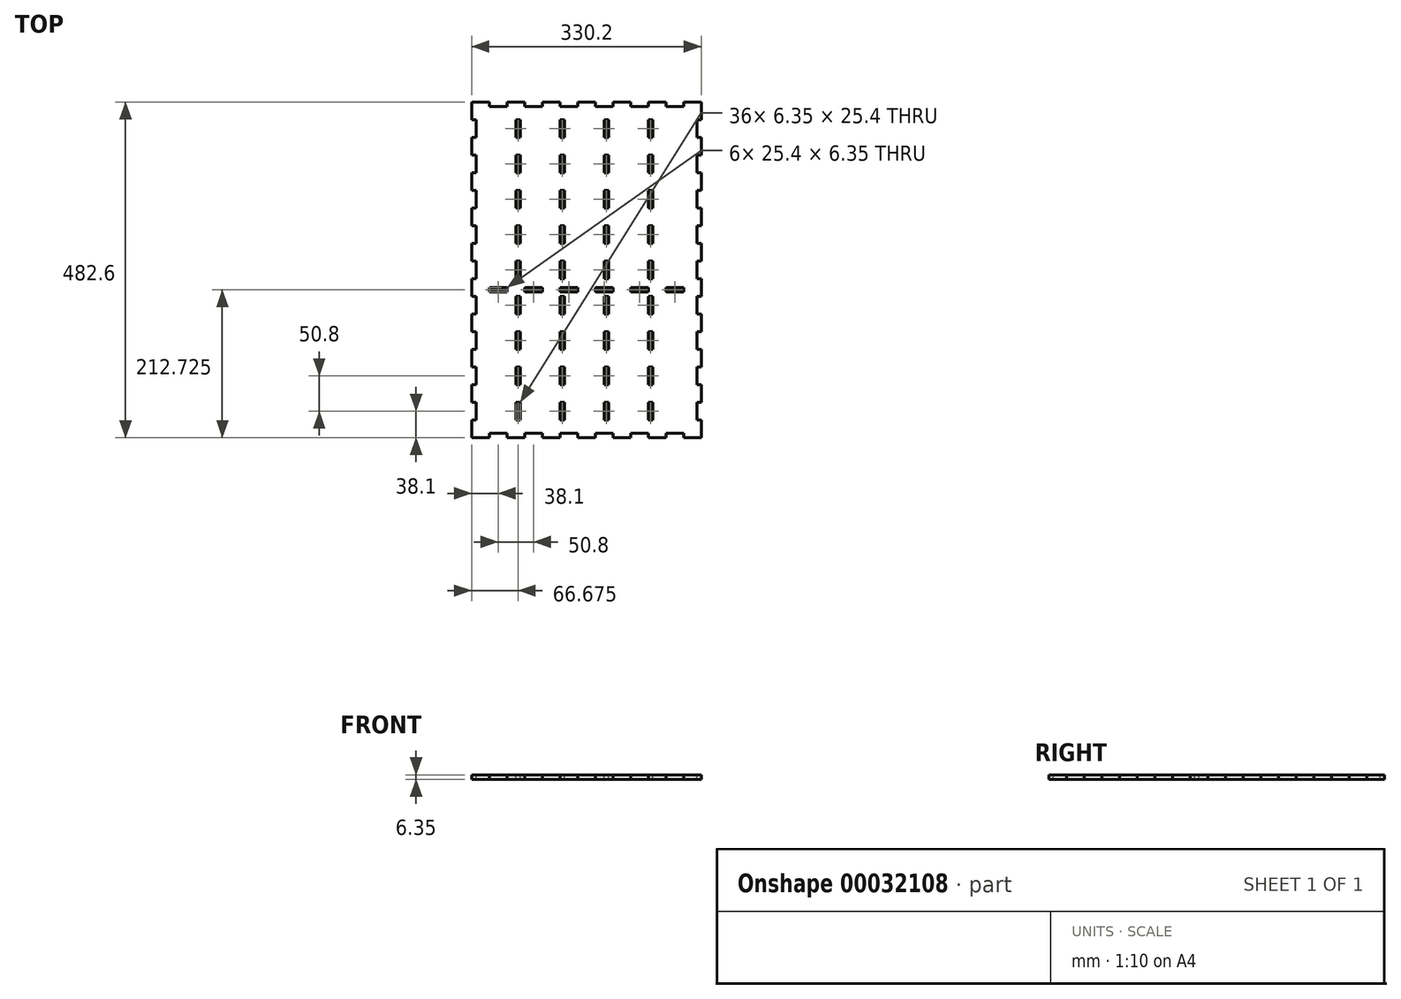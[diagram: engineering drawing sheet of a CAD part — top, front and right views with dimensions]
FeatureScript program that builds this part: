
annotation { "Feature Type Name" : "Feature", "Feature Type Description" : "" }
export const myFeature = defineFeature(function(context is Context, id is Id, definition is map)
    precondition{}
    {
        {
            var Q0;
            Q0=qCreatedBy(makeId("Top.planeOp"),FACE);
            var sketch = newSketch(context, id + "F0", { "sketchPlane" : qUnion([Q0])});
            skLineSegment(sketch, "E0.rect.bottom", {"start": v(165.1, 241.3) * mm, "end": v(-165.1, 241.3) * mm});
            skLineSegment(sketch, "E0.rect.top", {"start": v(165.1, -241.3) * mm, "end": v(-165.1, -241.3) * mm});
            skLineSegment(sketch, "E0.rect.left", {"start": v(165.1, 241.3) * mm, "end": v(165.1, -241.3) * mm});
            skLineSegment(sketch, "E0.rect.right", {"start": v(-165.1, 241.3) * mm, "end": v(-165.1, -241.3) * mm});
            skPoint(sketch, "E0.rect.middle", {"position": v(0, 0) * mm});
            skSolve(sketch);
        }
        {
            var Q0;
            Q0=makeQuery(id+"F0.imprint","IMPRINT",FACE,{"disambiguationData":[TD([[makeQuery(id+"F0.imprint","IMPRINT",EDGE,{"derivedFrom":sQuery(id+"F0.wireOp",EDGE,"E0.rect.bottom")}),1.0]])]});
            extrude(context, id + "F1", {"entities" : qUnion([Q0]), "depth" : 6.35 * mm});
        }
        {
            var Q0;
            Q0=makeQuery(id+"F1.opExtrude","CAP_FACE",FACE,{"disambiguationData":[OSD([sQuery(id+"F0.wireOp",EDGE,"E0.rect.bottom"),sQuery(id+"F0.wireOp",EDGE,"E0.rect.top"),sQuery(id+"F0.wireOp",EDGE,"E0.rect.left"),sQuery(id+"F0.wireOp",EDGE,"E0.rect.right")])],"isStart":false});
            var sketch = newSketch(context, id + "F2", { "sketchPlane" : qUnion([Q0])});
            skLineSegment(sketch, "E1.bottom", {"start": v(165.1, -215.9) * mm, "end": v(158.75, -215.9) * mm});
            skLineSegment(sketch, "E1.top", {"start": v(165.1, -190.5) * mm, "end": v(158.75, -190.5) * mm});
            skLineSegment(sketch, "E1.left", {"start": v(165.1, -215.9) * mm, "end": v(165.1, -190.5) * mm});
            skLineSegment(sketch, "E1.right", {"start": v(158.75, -215.9) * mm, "end": v(158.75, -190.5) * mm});
            skLineSegment(sketch, "E2.1.0.0", {"start": v(165.1, -165.1) * mm, "end": v(165.1, -139.7) * mm});
            skLineSegment(sketch, "E2.1.0.1", {"start": v(158.75, -165.1) * mm, "end": v(158.75, -139.7) * mm});
            skLineSegment(sketch, "E2.1.0.2", {"start": v(165.1, -165.1) * mm, "end": v(158.75, -165.1) * mm});
            skLineSegment(sketch, "E2.1.0.3", {"start": v(165.1, -139.7) * mm, "end": v(158.75, -139.7) * mm});
            skLineSegment(sketch, "E2.2.0.0", {"start": v(165.1, -114.3) * mm, "end": v(165.1, -88.9) * mm});
            skLineSegment(sketch, "E2.2.0.1", {"start": v(158.75, -114.3) * mm, "end": v(158.75, -88.9) * mm});
            skLineSegment(sketch, "E2.2.0.2", {"start": v(165.1, -114.3) * mm, "end": v(158.75, -114.3) * mm});
            skLineSegment(sketch, "E2.2.0.3", {"start": v(165.1, -88.9) * mm, "end": v(158.75, -88.9) * mm});
            skLineSegment(sketch, "E2.3.0.0", {"start": v(165.1, -63.5) * mm, "end": v(165.1, -38.1) * mm});
            skLineSegment(sketch, "E2.3.0.1", {"start": v(158.75, -63.5) * mm, "end": v(158.75, -38.1) * mm});
            skLineSegment(sketch, "E2.3.0.2", {"start": v(165.1, -63.5) * mm, "end": v(158.75, -63.5) * mm});
            skLineSegment(sketch, "E2.3.0.3", {"start": v(165.1, -38.1) * mm, "end": v(158.75, -38.1) * mm});
            skLineSegment(sketch, "E2.4.0.0", {"start": v(165.1, -12.7) * mm, "end": v(165.1, 12.7) * mm});
            skLineSegment(sketch, "E2.4.0.1", {"start": v(158.75, -12.7) * mm, "end": v(158.75, 12.7) * mm});
            skLineSegment(sketch, "E2.4.0.2", {"start": v(165.1, -12.7) * mm, "end": v(158.75, -12.7) * mm});
            skLineSegment(sketch, "E2.4.0.3", {"start": v(165.1, 12.7) * mm, "end": v(158.75, 12.7) * mm});
            skLineSegment(sketch, "E2.5.0.0", {"start": v(165.1, 38.1) * mm, "end": v(165.1, 63.5) * mm});
            skLineSegment(sketch, "E2.5.0.1", {"start": v(158.75, 38.1) * mm, "end": v(158.75, 63.5) * mm});
            skLineSegment(sketch, "E2.5.0.2", {"start": v(165.1, 38.1) * mm, "end": v(158.75, 38.1) * mm});
            skLineSegment(sketch, "E2.5.0.3", {"start": v(165.1, 63.5) * mm, "end": v(158.75, 63.5) * mm});
            skLineSegment(sketch, "E2.6.0.0", {"start": v(165.1, 88.9) * mm, "end": v(165.1, 114.3) * mm});
            skLineSegment(sketch, "E2.6.0.1", {"start": v(158.75, 88.9) * mm, "end": v(158.75, 114.3) * mm});
            skLineSegment(sketch, "E2.6.0.2", {"start": v(165.1, 88.9) * mm, "end": v(158.75, 88.9) * mm});
            skLineSegment(sketch, "E2.6.0.3", {"start": v(165.1, 114.3) * mm, "end": v(158.75, 114.3) * mm});
            skLineSegment(sketch, "E2.7.0.0", {"start": v(165.1, 139.7) * mm, "end": v(165.1, 165.1) * mm});
            skLineSegment(sketch, "E2.7.0.1", {"start": v(158.75, 139.7) * mm, "end": v(158.75, 165.1) * mm});
            skLineSegment(sketch, "E2.7.0.2", {"start": v(165.1, 139.7) * mm, "end": v(158.75, 139.7) * mm});
            skLineSegment(sketch, "E2.7.0.3", {"start": v(165.1, 165.1) * mm, "end": v(158.75, 165.1) * mm});
            skLineSegment(sketch, "E2.8.0.0", {"start": v(165.1, 190.5) * mm, "end": v(165.1, 215.9) * mm});
            skLineSegment(sketch, "E2.8.0.1", {"start": v(158.75, 190.5) * mm, "end": v(158.75, 215.9) * mm});
            skLineSegment(sketch, "E2.8.0.2", {"start": v(165.1, 190.5) * mm, "end": v(158.75, 190.5) * mm});
            skLineSegment(sketch, "E2.8.0.3", {"start": v(165.1, 215.9) * mm, "end": v(158.75, 215.9) * mm});
            skLineSegment(sketch, "E2.direction1", {"start": v(165.1, -215.9) * mm, "end": v(165.1, -165.1) * mm, "construction": true});
            skLineSegment(sketch, "E3", {"start": v(0, -241.3) * mm, "end": v(0, 241.3) * mm, "construction": true});
            skLineSegment(sketch, "E4.MirrorCS", {"start": v(-165.1, -215.9) * mm, "end": v(-158.75, -215.9) * mm});
            skLineSegment(sketch, "E5.MirrorCS", {"start": v(-165.1, -165.1) * mm, "end": v(-158.75, -165.1) * mm});
            skLineSegment(sketch, "E6.MirrorCS", {"start": v(-165.1, 12.7) * mm, "end": v(-158.75, 12.7) * mm});
            skLineSegment(sketch, "E7.MirrorCS", {"start": v(-165.1, -63.5) * mm, "end": v(-158.75, -63.5) * mm});
            skLineSegment(sketch, "E8.MirrorCS", {"start": v(-165.1, 63.5) * mm, "end": v(-158.75, 63.5) * mm});
            skLineSegment(sketch, "E9.MirrorCS", {"start": v(-165.1, -38.1) * mm, "end": v(-158.75, -38.1) * mm});
            skLineSegment(sketch, "E10.MirrorCS", {"start": v(-165.1, 38.1) * mm, "end": v(-158.75, 38.1) * mm});
            skLineSegment(sketch, "E11.MirrorCS", {"start": v(-165.1, -190.5) * mm, "end": v(-158.75, -190.5) * mm});
            skLineSegment(sketch, "E12.MirrorCS", {"start": v(-165.1, 215.9) * mm, "end": v(-158.75, 215.9) * mm});
            skLineSegment(sketch, "E13.MirrorCS", {"start": v(-165.1, 114.3) * mm, "end": v(-158.75, 114.3) * mm});
            skLineSegment(sketch, "E14.MirrorCS", {"start": v(-165.1, -12.7) * mm, "end": v(-158.75, -12.7) * mm});
            skLineSegment(sketch, "E15.MirrorCS", {"start": v(-165.1, 190.5) * mm, "end": v(-158.75, 190.5) * mm});
            skLineSegment(sketch, "E16.MirrorCS", {"start": v(-165.1, 88.9) * mm, "end": v(-158.75, 88.9) * mm});
            skLineSegment(sketch, "E17.MirrorCS", {"start": v(-165.1, -88.9) * mm, "end": v(-158.75, -88.9) * mm});
            skLineSegment(sketch, "E18.MirrorCS", {"start": v(-165.1, -139.7) * mm, "end": v(-158.75, -139.7) * mm});
            skLineSegment(sketch, "E19.MirrorCS", {"start": v(-165.1, -114.3) * mm, "end": v(-158.75, -114.3) * mm});
            skLineSegment(sketch, "E20.MirrorCS", {"start": v(-165.1, 139.7) * mm, "end": v(-158.75, 139.7) * mm});
            skLineSegment(sketch, "E21.MirrorCS", {"start": v(-165.1, 165.1) * mm, "end": v(-158.75, 165.1) * mm});
            skLineSegment(sketch, "E22.MirrorCS", {"start": v(-165.1, 88.9) * mm, "end": v(-165.1, 114.3) * mm});
            skLineSegment(sketch, "E23.MirrorCS", {"start": v(-158.75, 190.5) * mm, "end": v(-158.75, 215.9) * mm});
            skLineSegment(sketch, "E24.MirrorCS", {"start": v(-158.75, -12.7) * mm, "end": v(-158.75, 12.7) * mm});
            skLineSegment(sketch, "E25.MirrorCS", {"start": v(-165.1, -12.7) * mm, "end": v(-165.1, 12.7) * mm});
            skLineSegment(sketch, "E26.MirrorCS", {"start": v(-158.75, -63.5) * mm, "end": v(-158.75, -38.1) * mm});
            skLineSegment(sketch, "E27.MirrorCS", {"start": v(-165.1, 190.5) * mm, "end": v(-165.1, 215.9) * mm});
            skLineSegment(sketch, "E28.MirrorCS", {"start": v(-165.1, -215.9) * mm, "end": v(-165.1, -190.5) * mm});
            skLineSegment(sketch, "E29.MirrorCS", {"start": v(-158.75, -215.9) * mm, "end": v(-158.75, -190.5) * mm});
            skLineSegment(sketch, "E30.MirrorCS", {"start": v(-165.1, -114.3) * mm, "end": v(-165.1, -88.9) * mm});
            skLineSegment(sketch, "E31.MirrorCS", {"start": v(-165.1, 38.1) * mm, "end": v(-165.1, 63.5) * mm});
            skLineSegment(sketch, "E32.MirrorCS", {"start": v(-158.75, 38.1) * mm, "end": v(-158.75, 63.5) * mm});
            skLineSegment(sketch, "E33.MirrorCS", {"start": v(-165.1, -63.5) * mm, "end": v(-165.1, -38.1) * mm});
            skLineSegment(sketch, "E34.MirrorCS", {"start": v(-165.1, 139.7) * mm, "end": v(-165.1, 165.1) * mm});
            skLineSegment(sketch, "E35.MirrorCS", {"start": v(-158.75, 88.9) * mm, "end": v(-158.75, 114.3) * mm});
            skLineSegment(sketch, "E36.MirrorCS", {"start": v(-158.75, -114.3) * mm, "end": v(-158.75, -88.9) * mm});
            skLineSegment(sketch, "E37.MirrorCS", {"start": v(-158.75, -165.1) * mm, "end": v(-158.75, -139.7) * mm});
            skLineSegment(sketch, "E38.MirrorCS", {"start": v(-165.1, -165.1) * mm, "end": v(-165.1, -139.7) * mm});
            skLineSegment(sketch, "E39.MirrorCS", {"start": v(-158.75, 139.7) * mm, "end": v(-158.75, 165.1) * mm});
            skLineSegment(sketch, "E40.bottom", {"start": v(-139.7, -241.3) * mm, "end": v(-114.3, -241.3) * mm});
            skLineSegment(sketch, "E40.top", {"start": v(-139.7, -234.95) * mm, "end": v(-114.3, -234.95) * mm});
            skLineSegment(sketch, "E40.left", {"start": v(-139.7, -241.3) * mm, "end": v(-139.7, -234.95) * mm});
            skLineSegment(sketch, "E40.right", {"start": v(-114.3, -241.3) * mm, "end": v(-114.3, -234.95) * mm});
            skLineSegment(sketch, "E41", {"start": v(-165.1, 0) * mm, "end": v(165.1, 0) * mm, "construction": true});
            skLineSegment(sketch, "E42.0.1.0", {"start": v(-139.7, -31.75) * mm, "end": v(-139.7, -25.4) * mm});
            skLineSegment(sketch, "E42.0.1.1", {"start": v(-114.3, -31.75) * mm, "end": v(-114.3, -25.4) * mm});
            skLineSegment(sketch, "E42.0.1.2", {"start": v(-139.7, -25.4) * mm, "end": v(-114.3, -25.4) * mm});
            skLineSegment(sketch, "E42.0.1.3", {"start": v(-139.7, -31.75) * mm, "end": v(-114.3, -31.75) * mm});
            skLineSegment(sketch, "E42.1.0.0", {"start": v(-88.9, -241.3) * mm, "end": v(-88.9, -234.95) * mm});
            skLineSegment(sketch, "E42.1.0.1", {"start": v(-63.5, -241.3) * mm, "end": v(-63.5, -234.95) * mm});
            skLineSegment(sketch, "E42.1.0.2", {"start": v(-88.9, -234.95) * mm, "end": v(-63.5, -234.95) * mm});
            skLineSegment(sketch, "E42.1.0.3", {"start": v(-88.9, -241.3) * mm, "end": v(-63.5, -241.3) * mm});
            skLineSegment(sketch, "E42.1.1.0", {"start": v(-88.9, -31.75) * mm, "end": v(-88.9, -25.4) * mm});
            skLineSegment(sketch, "E42.1.1.1", {"start": v(-63.5, -31.75) * mm, "end": v(-63.5, -25.4) * mm});
            skLineSegment(sketch, "E42.1.1.2", {"start": v(-88.9, -25.4) * mm, "end": v(-63.5, -25.4) * mm});
            skLineSegment(sketch, "E42.1.1.3", {"start": v(-88.9, -31.75) * mm, "end": v(-63.5, -31.75) * mm});
            skLineSegment(sketch, "E42.2.0.0", {"start": v(-38.1, -241.3) * mm, "end": v(-38.1, -234.95) * mm});
            skLineSegment(sketch, "E42.2.0.1", {"start": v(-12.7, -241.3) * mm, "end": v(-12.7, -234.95) * mm});
            skLineSegment(sketch, "E42.2.0.2", {"start": v(-38.1, -234.95) * mm, "end": v(-12.7, -234.95) * mm});
            skLineSegment(sketch, "E42.2.0.3", {"start": v(-38.1, -241.3) * mm, "end": v(-12.7, -241.3) * mm});
            skLineSegment(sketch, "E42.2.1.0", {"start": v(-38.1, -31.75) * mm, "end": v(-38.1, -25.4) * mm});
            skLineSegment(sketch, "E42.2.1.1", {"start": v(-12.7, -31.75) * mm, "end": v(-12.7, -25.4) * mm});
            skLineSegment(sketch, "E42.2.1.2", {"start": v(-38.1, -25.4) * mm, "end": v(-12.7, -25.4) * mm});
            skLineSegment(sketch, "E42.2.1.3", {"start": v(-38.1, -31.75) * mm, "end": v(-12.7, -31.75) * mm});
            skLineSegment(sketch, "E42.3.0.0", {"start": v(12.7, -241.3) * mm, "end": v(12.7, -234.95) * mm});
            skLineSegment(sketch, "E42.3.0.1", {"start": v(38.1, -241.3) * mm, "end": v(38.1, -234.95) * mm});
            skLineSegment(sketch, "E42.3.0.2", {"start": v(12.7, -234.95) * mm, "end": v(38.1, -234.95) * mm});
            skLineSegment(sketch, "E42.3.0.3", {"start": v(12.7, -241.3) * mm, "end": v(38.1, -241.3) * mm});
            skLineSegment(sketch, "E42.3.1.0", {"start": v(12.7, -31.75) * mm, "end": v(12.7, -25.4) * mm});
            skLineSegment(sketch, "E42.3.1.1", {"start": v(38.1, -31.75) * mm, "end": v(38.1, -25.4) * mm});
            skLineSegment(sketch, "E42.3.1.2", {"start": v(12.7, -25.4) * mm, "end": v(38.1, -25.4) * mm});
            skLineSegment(sketch, "E42.3.1.3", {"start": v(12.7, -31.75) * mm, "end": v(38.1, -31.75) * mm});
            skLineSegment(sketch, "E42.4.0.0", {"start": v(63.5, -241.3) * mm, "end": v(63.5, -234.95) * mm});
            skLineSegment(sketch, "E42.4.0.1", {"start": v(88.9, -241.3) * mm, "end": v(88.9, -234.95) * mm});
            skLineSegment(sketch, "E42.4.0.2", {"start": v(63.5, -234.95) * mm, "end": v(88.9, -234.95) * mm});
            skLineSegment(sketch, "E42.4.0.3", {"start": v(63.5, -241.3) * mm, "end": v(88.9, -241.3) * mm});
            skLineSegment(sketch, "E42.4.1.0", {"start": v(63.5, -31.75) * mm, "end": v(63.5, -25.4) * mm});
            skLineSegment(sketch, "E42.4.1.1", {"start": v(88.9, -31.75) * mm, "end": v(88.9, -25.4) * mm});
            skLineSegment(sketch, "E42.4.1.2", {"start": v(63.5, -25.4) * mm, "end": v(88.9, -25.4) * mm});
            skLineSegment(sketch, "E42.4.1.3", {"start": v(63.5, -31.75) * mm, "end": v(88.9, -31.75) * mm});
            skLineSegment(sketch, "E42.5.0.0", {"start": v(114.3, -241.3) * mm, "end": v(114.3, -234.95) * mm});
            skLineSegment(sketch, "E42.5.0.1", {"start": v(139.7, -241.3) * mm, "end": v(139.7, -234.95) * mm});
            skLineSegment(sketch, "E42.5.0.2", {"start": v(114.3, -234.95) * mm, "end": v(139.7, -234.95) * mm});
            skLineSegment(sketch, "E42.5.0.3", {"start": v(114.3, -241.3) * mm, "end": v(139.7, -241.3) * mm});
            skLineSegment(sketch, "E42.5.1.0", {"start": v(114.3, -31.75) * mm, "end": v(114.3, -25.4) * mm});
            skLineSegment(sketch, "E42.5.1.1", {"start": v(139.7, -31.75) * mm, "end": v(139.7, -25.4) * mm});
            skLineSegment(sketch, "E42.5.1.2", {"start": v(114.3, -25.4) * mm, "end": v(139.7, -25.4) * mm});
            skLineSegment(sketch, "E42.5.1.3", {"start": v(114.3, -31.75) * mm, "end": v(139.7, -31.75) * mm});
            skLineSegment(sketch, "E42.direction1", {"start": v(-139.7, -241.3) * mm, "end": v(-88.9, -241.3) * mm, "construction": true});
            skLineSegment(sketch, "E42.direction2", {"start": v(-139.7, -241.3) * mm, "end": v(-139.7, -31.75) * mm, "construction": true});
            skLineSegment(sketch, "E43.MirrorCS", {"start": v(-139.7, 241.3) * mm, "end": v(-139.7, 234.95) * mm});
            skLineSegment(sketch, "E44.MirrorCS", {"start": v(-88.9, 241.3) * mm, "end": v(-88.9, 234.95) * mm});
            skLineSegment(sketch, "E45.MirrorCS", {"start": v(-12.7, 241.3) * mm, "end": v(-12.7, 234.95) * mm});
            skLineSegment(sketch, "E46.MirrorCS", {"start": v(88.9, 241.3) * mm, "end": v(88.9, 234.95) * mm});
            skLineSegment(sketch, "E47.MirrorCS", {"start": v(139.7, 241.3) * mm, "end": v(139.7, 234.95) * mm});
            skLineSegment(sketch, "E48.MirrorCS", {"start": v(38.1, 241.3) * mm, "end": v(38.1, 234.95) * mm});
            skLineSegment(sketch, "E49.MirrorCS", {"start": v(-63.5, 241.3) * mm, "end": v(-63.5, 234.95) * mm});
            skLineSegment(sketch, "E50.MirrorCS", {"start": v(-114.3, 241.3) * mm, "end": v(-114.3, 234.95) * mm});
            skLineSegment(sketch, "E51.MirrorCS", {"start": v(114.3, 241.3) * mm, "end": v(114.3, 234.95) * mm});
            skLineSegment(sketch, "E52.MirrorCS", {"start": v(-38.1, 241.3) * mm, "end": v(-38.1, 234.95) * mm});
            skLineSegment(sketch, "E53.MirrorCS", {"start": v(12.7, 241.3) * mm, "end": v(12.7, 234.95) * mm});
            skLineSegment(sketch, "E54.MirrorCS", {"start": v(63.5, 241.3) * mm, "end": v(63.5, 234.95) * mm});
            skLineSegment(sketch, "E55.MirrorCS", {"start": v(-38.1, 241.3) * mm, "end": v(-12.7, 241.3) * mm});
            skLineSegment(sketch, "E56.MirrorCS", {"start": v(114.3, 241.3) * mm, "end": v(139.7, 241.3) * mm});
            skLineSegment(sketch, "E57.MirrorCS", {"start": v(63.5, 234.95) * mm, "end": v(88.9, 234.95) * mm});
            skLineSegment(sketch, "E58.MirrorCS", {"start": v(0, 241.3) * mm, "end": v(0, -241.3) * mm});
            skLineSegment(sketch, "E59.MirrorCS", {"start": v(-139.7, 234.95) * mm, "end": v(-114.3, 234.95) * mm});
            skLineSegment(sketch, "E60.MirrorCS", {"start": v(-139.7, 241.3) * mm, "end": v(-114.3, 241.3) * mm});
            skLineSegment(sketch, "E61.MirrorCS", {"start": v(114.3, 234.95) * mm, "end": v(139.7, 234.95) * mm});
            skLineSegment(sketch, "E62.MirrorCS", {"start": v(12.7, 234.95) * mm, "end": v(38.1, 234.95) * mm});
            skLineSegment(sketch, "E63.MirrorCS", {"start": v(-88.9, 234.95) * mm, "end": v(-63.5, 234.95) * mm});
            skLineSegment(sketch, "E64.MirrorCS", {"start": v(-88.9, 241.3) * mm, "end": v(-63.5, 241.3) * mm});
            skLineSegment(sketch, "E65.MirrorCS", {"start": v(12.7, 241.3) * mm, "end": v(38.1, 241.3) * mm});
            skLineSegment(sketch, "E66.MirrorCS", {"start": v(63.5, 241.3) * mm, "end": v(88.9, 241.3) * mm});
            skLineSegment(sketch, "E67.MirrorCS", {"start": v(-38.1, 234.95) * mm, "end": v(-12.7, 234.95) * mm});
            skSolve(sketch);
        }
        {
            var Q0;
            Q0 = qSketchRegion(id + "F2", true);
            extrude(context, id + "F3", {"entities" : qUnion([Q0]), "operationType" : NewBodyOperationType.REMOVE, "endBound" : BoundingType.UP_TO_NEXT, "oppositeDirection" : true, "depth" : 25.4 * mm});
        }
        {
            var Q0;
            Q0=makeQuery(id+"F1.opExtrude","CAP_FACE",FACE,{"disambiguationData":[OSD([sQuery(id+"F0.wireOp",EDGE,"E0.rect.bottom"),sQuery(id+"F0.wireOp",EDGE,"E0.rect.top"),sQuery(id+"F0.wireOp",EDGE,"E0.rect.left"),sQuery(id+"F0.wireOp",EDGE,"E0.rect.right")])],"isStart":false});
            var sketch = newSketch(context, id + "F4", { "sketchPlane" : qUnion([Q0])});
            skLineSegment(sketch, "E68.bottom", {"start": v(-101.6, -215.9) * mm, "end": v(-95.25, -215.9) * mm});
            skLineSegment(sketch, "E68.top", {"start": v(-101.6, -190.5) * mm, "end": v(-95.25, -190.5) * mm});
            skLineSegment(sketch, "E68.left", {"start": v(-101.6, -215.9) * mm, "end": v(-101.6, -190.5) * mm});
            skLineSegment(sketch, "E68.right", {"start": v(-95.25, -215.9) * mm, "end": v(-95.25, -190.5) * mm});
            skPoint(sketch, "E69", {"position": v(-98.43, -215.9) * mm});
            skPoint(sketch, "E70.0.1.0", {"position": v(-98.43, -165.1) * mm});
            skLineSegment(sketch, "E70.0.1.1", {"start": v(-95.25, -165.1) * mm, "end": v(-95.25, -139.7) * mm});
            skLineSegment(sketch, "E70.0.1.2", {"start": v(-101.6, -165.1) * mm, "end": v(-101.6, -139.7) * mm});
            skLineSegment(sketch, "E70.0.1.3", {"start": v(-101.6, -139.7) * mm, "end": v(-95.25, -139.7) * mm});
            skLineSegment(sketch, "E70.0.1.4", {"start": v(-101.6, -165.1) * mm, "end": v(-95.25, -165.1) * mm});
            skPoint(sketch, "E70.0.2.0", {"position": v(-98.43, -114.3) * mm});
            skLineSegment(sketch, "E70.0.2.1", {"start": v(-95.25, -114.3) * mm, "end": v(-95.25, -88.9) * mm});
            skLineSegment(sketch, "E70.0.2.2", {"start": v(-101.6, -114.3) * mm, "end": v(-101.6, -88.9) * mm});
            skLineSegment(sketch, "E70.0.2.3", {"start": v(-101.6, -88.9) * mm, "end": v(-95.25, -88.9) * mm});
            skLineSegment(sketch, "E70.0.2.4", {"start": v(-101.6, -114.3) * mm, "end": v(-95.25, -114.3) * mm});
            skPoint(sketch, "E70.0.3.0", {"position": v(-98.43, -63.5) * mm});
            skLineSegment(sketch, "E70.0.3.1", {"start": v(-95.25, -63.5) * mm, "end": v(-95.25, -38.1) * mm});
            skLineSegment(sketch, "E70.0.3.2", {"start": v(-101.6, -63.5) * mm, "end": v(-101.6, -38.1) * mm});
            skLineSegment(sketch, "E70.0.3.3", {"start": v(-101.6, -38.1) * mm, "end": v(-95.25, -38.1) * mm});
            skLineSegment(sketch, "E70.0.3.4", {"start": v(-101.6, -63.5) * mm, "end": v(-95.25, -63.5) * mm});
            skPoint(sketch, "E70.0.4.0", {"position": v(-98.43, -12.7) * mm});
            skLineSegment(sketch, "E70.0.4.1", {"start": v(-95.25, -12.7) * mm, "end": v(-95.25, 12.7) * mm});
            skLineSegment(sketch, "E70.0.4.2", {"start": v(-101.6, -12.7) * mm, "end": v(-101.6, 12.7) * mm});
            skLineSegment(sketch, "E70.0.4.3", {"start": v(-101.6, 12.7) * mm, "end": v(-95.25, 12.7) * mm});
            skLineSegment(sketch, "E70.0.4.4", {"start": v(-101.6, -12.7) * mm, "end": v(-95.25, -12.7) * mm});
            skPoint(sketch, "E70.0.5.0", {"position": v(-98.43, 38.1) * mm});
            skLineSegment(sketch, "E70.0.5.1", {"start": v(-95.25, 38.1) * mm, "end": v(-95.25, 63.5) * mm});
            skLineSegment(sketch, "E70.0.5.2", {"start": v(-101.6, 38.1) * mm, "end": v(-101.6, 63.5) * mm});
            skLineSegment(sketch, "E70.0.5.3", {"start": v(-101.6, 63.5) * mm, "end": v(-95.25, 63.5) * mm});
            skLineSegment(sketch, "E70.0.5.4", {"start": v(-101.6, 38.1) * mm, "end": v(-95.25, 38.1) * mm});
            skPoint(sketch, "E70.0.6.0", {"position": v(-98.43, 88.9) * mm});
            skLineSegment(sketch, "E70.0.6.1", {"start": v(-95.25, 88.9) * mm, "end": v(-95.25, 114.3) * mm});
            skLineSegment(sketch, "E70.0.6.2", {"start": v(-101.6, 88.9) * mm, "end": v(-101.6, 114.3) * mm});
            skLineSegment(sketch, "E70.0.6.3", {"start": v(-101.6, 114.3) * mm, "end": v(-95.25, 114.3) * mm});
            skLineSegment(sketch, "E70.0.6.4", {"start": v(-101.6, 88.9) * mm, "end": v(-95.25, 88.9) * mm});
            skPoint(sketch, "E70.0.7.0", {"position": v(-98.43, 139.7) * mm});
            skLineSegment(sketch, "E70.0.7.1", {"start": v(-95.25, 139.7) * mm, "end": v(-95.25, 165.1) * mm});
            skLineSegment(sketch, "E70.0.7.2", {"start": v(-101.6, 139.7) * mm, "end": v(-101.6, 165.1) * mm});
            skLineSegment(sketch, "E70.0.7.3", {"start": v(-101.6, 165.1) * mm, "end": v(-95.25, 165.1) * mm});
            skLineSegment(sketch, "E70.0.7.4", {"start": v(-101.6, 139.7) * mm, "end": v(-95.25, 139.7) * mm});
            skPoint(sketch, "E70.0.8.0", {"position": v(-98.43, 190.5) * mm});
            skLineSegment(sketch, "E70.0.8.1", {"start": v(-95.25, 190.5) * mm, "end": v(-95.25, 215.9) * mm});
            skLineSegment(sketch, "E70.0.8.2", {"start": v(-101.6, 190.5) * mm, "end": v(-101.6, 215.9) * mm});
            skLineSegment(sketch, "E70.0.8.3", {"start": v(-101.6, 215.9) * mm, "end": v(-95.25, 215.9) * mm});
            skLineSegment(sketch, "E70.0.8.4", {"start": v(-101.6, 190.5) * mm, "end": v(-95.25, 190.5) * mm});
            skPoint(sketch, "E70.1.0.0", {"position": v(-34.93, -215.9) * mm});
            skLineSegment(sketch, "E70.1.0.1", {"start": v(-31.75, -215.9) * mm, "end": v(-31.75, -190.5) * mm});
            skLineSegment(sketch, "E70.1.0.2", {"start": v(-38.1, -215.9) * mm, "end": v(-38.1, -190.5) * mm});
            skLineSegment(sketch, "E70.1.0.3", {"start": v(-38.1, -190.5) * mm, "end": v(-31.75, -190.5) * mm});
            skLineSegment(sketch, "E70.1.0.4", {"start": v(-38.1, -215.9) * mm, "end": v(-31.75, -215.9) * mm});
            skPoint(sketch, "E70.1.1.0", {"position": v(-34.93, -165.1) * mm});
            skLineSegment(sketch, "E70.1.1.1", {"start": v(-31.75, -165.1) * mm, "end": v(-31.75, -139.7) * mm});
            skLineSegment(sketch, "E70.1.1.2", {"start": v(-38.1, -165.1) * mm, "end": v(-38.1, -139.7) * mm});
            skLineSegment(sketch, "E70.1.1.3", {"start": v(-38.1, -139.7) * mm, "end": v(-31.75, -139.7) * mm});
            skLineSegment(sketch, "E70.1.1.4", {"start": v(-38.1, -165.1) * mm, "end": v(-31.75, -165.1) * mm});
            skPoint(sketch, "E70.1.2.0", {"position": v(-34.93, -114.3) * mm});
            skLineSegment(sketch, "E70.1.2.1", {"start": v(-31.75, -114.3) * mm, "end": v(-31.75, -88.9) * mm});
            skLineSegment(sketch, "E70.1.2.2", {"start": v(-38.1, -114.3) * mm, "end": v(-38.1, -88.9) * mm});
            skLineSegment(sketch, "E70.1.2.3", {"start": v(-38.1, -88.9) * mm, "end": v(-31.75, -88.9) * mm});
            skLineSegment(sketch, "E70.1.2.4", {"start": v(-38.1, -114.3) * mm, "end": v(-31.75, -114.3) * mm});
            skPoint(sketch, "E70.1.3.0", {"position": v(-34.93, -63.5) * mm});
            skLineSegment(sketch, "E70.1.3.1", {"start": v(-31.75, -63.5) * mm, "end": v(-31.75, -38.1) * mm});
            skLineSegment(sketch, "E70.1.3.2", {"start": v(-38.1, -63.5) * mm, "end": v(-38.1, -38.1) * mm});
            skLineSegment(sketch, "E70.1.3.3", {"start": v(-38.1, -38.1) * mm, "end": v(-31.75, -38.1) * mm});
            skLineSegment(sketch, "E70.1.3.4", {"start": v(-38.1, -63.5) * mm, "end": v(-31.75, -63.5) * mm});
            skPoint(sketch, "E70.1.4.0", {"position": v(-34.93, -12.7) * mm});
            skLineSegment(sketch, "E70.1.4.1", {"start": v(-31.75, -12.7) * mm, "end": v(-31.75, 12.7) * mm});
            skLineSegment(sketch, "E70.1.4.2", {"start": v(-38.1, -12.7) * mm, "end": v(-38.1, 12.7) * mm});
            skLineSegment(sketch, "E70.1.4.3", {"start": v(-38.1, 12.7) * mm, "end": v(-31.75, 12.7) * mm});
            skLineSegment(sketch, "E70.1.4.4", {"start": v(-38.1, -12.7) * mm, "end": v(-31.75, -12.7) * mm});
            skPoint(sketch, "E70.1.5.0", {"position": v(-34.93, 38.1) * mm});
            skLineSegment(sketch, "E70.1.5.1", {"start": v(-31.75, 38.1) * mm, "end": v(-31.75, 63.5) * mm});
            skLineSegment(sketch, "E70.1.5.2", {"start": v(-38.1, 38.1) * mm, "end": v(-38.1, 63.5) * mm});
            skLineSegment(sketch, "E70.1.5.3", {"start": v(-38.1, 63.5) * mm, "end": v(-31.75, 63.5) * mm});
            skLineSegment(sketch, "E70.1.5.4", {"start": v(-38.1, 38.1) * mm, "end": v(-31.75, 38.1) * mm});
            skPoint(sketch, "E70.1.6.0", {"position": v(-34.93, 88.9) * mm});
            skLineSegment(sketch, "E70.1.6.1", {"start": v(-31.75, 88.9) * mm, "end": v(-31.75, 114.3) * mm});
            skLineSegment(sketch, "E70.1.6.2", {"start": v(-38.1, 88.9) * mm, "end": v(-38.1, 114.3) * mm});
            skLineSegment(sketch, "E70.1.6.3", {"start": v(-38.1, 114.3) * mm, "end": v(-31.75, 114.3) * mm});
            skLineSegment(sketch, "E70.1.6.4", {"start": v(-38.1, 88.9) * mm, "end": v(-31.75, 88.9) * mm});
            skPoint(sketch, "E70.1.7.0", {"position": v(-34.93, 139.7) * mm});
            skLineSegment(sketch, "E70.1.7.1", {"start": v(-31.75, 139.7) * mm, "end": v(-31.75, 165.1) * mm});
            skLineSegment(sketch, "E70.1.7.2", {"start": v(-38.1, 139.7) * mm, "end": v(-38.1, 165.1) * mm});
            skLineSegment(sketch, "E70.1.7.3", {"start": v(-38.1, 165.1) * mm, "end": v(-31.75, 165.1) * mm});
            skLineSegment(sketch, "E70.1.7.4", {"start": v(-38.1, 139.7) * mm, "end": v(-31.75, 139.7) * mm});
            skPoint(sketch, "E70.1.8.0", {"position": v(-34.93, 190.5) * mm});
            skLineSegment(sketch, "E70.1.8.1", {"start": v(-31.75, 190.5) * mm, "end": v(-31.75, 215.9) * mm});
            skLineSegment(sketch, "E70.1.8.2", {"start": v(-38.1, 190.5) * mm, "end": v(-38.1, 215.9) * mm});
            skLineSegment(sketch, "E70.1.8.3", {"start": v(-38.1, 215.9) * mm, "end": v(-31.75, 215.9) * mm});
            skLineSegment(sketch, "E70.1.8.4", {"start": v(-38.1, 190.5) * mm, "end": v(-31.75, 190.5) * mm});
            skPoint(sketch, "E70.2.0.0", {"position": v(28.57, -215.9) * mm});
            skLineSegment(sketch, "E70.2.0.1", {"start": v(31.75, -215.9) * mm, "end": v(31.75, -190.5) * mm});
            skLineSegment(sketch, "E70.2.0.2", {"start": v(25.4, -215.9) * mm, "end": v(25.4, -190.5) * mm});
            skLineSegment(sketch, "E70.2.0.3", {"start": v(25.4, -190.5) * mm, "end": v(31.75, -190.5) * mm});
            skLineSegment(sketch, "E70.2.0.4", {"start": v(25.4, -215.9) * mm, "end": v(31.75, -215.9) * mm});
            skPoint(sketch, "E70.2.1.0", {"position": v(28.57, -165.1) * mm});
            skLineSegment(sketch, "E70.2.1.1", {"start": v(31.75, -165.1) * mm, "end": v(31.75, -139.7) * mm});
            skLineSegment(sketch, "E70.2.1.2", {"start": v(25.4, -165.1) * mm, "end": v(25.4, -139.7) * mm});
            skLineSegment(sketch, "E70.2.1.3", {"start": v(25.4, -139.7) * mm, "end": v(31.75, -139.7) * mm});
            skLineSegment(sketch, "E70.2.1.4", {"start": v(25.4, -165.1) * mm, "end": v(31.75, -165.1) * mm});
            skPoint(sketch, "E70.2.2.0", {"position": v(28.57, -114.3) * mm});
            skLineSegment(sketch, "E70.2.2.1", {"start": v(31.75, -114.3) * mm, "end": v(31.75, -88.9) * mm});
            skLineSegment(sketch, "E70.2.2.2", {"start": v(25.4, -114.3) * mm, "end": v(25.4, -88.9) * mm});
            skLineSegment(sketch, "E70.2.2.3", {"start": v(25.4, -88.9) * mm, "end": v(31.75, -88.9) * mm});
            skLineSegment(sketch, "E70.2.2.4", {"start": v(25.4, -114.3) * mm, "end": v(31.75, -114.3) * mm});
            skPoint(sketch, "E70.2.3.0", {"position": v(28.57, -63.5) * mm});
            skLineSegment(sketch, "E70.2.3.1", {"start": v(31.75, -63.5) * mm, "end": v(31.75, -38.1) * mm});
            skLineSegment(sketch, "E70.2.3.2", {"start": v(25.4, -63.5) * mm, "end": v(25.4, -38.1) * mm});
            skLineSegment(sketch, "E70.2.3.3", {"start": v(25.4, -38.1) * mm, "end": v(31.75, -38.1) * mm});
            skLineSegment(sketch, "E70.2.3.4", {"start": v(25.4, -63.5) * mm, "end": v(31.75, -63.5) * mm});
            skPoint(sketch, "E70.2.4.0", {"position": v(28.57, -12.7) * mm});
            skLineSegment(sketch, "E70.2.4.1", {"start": v(31.75, -12.7) * mm, "end": v(31.75, 12.7) * mm});
            skLineSegment(sketch, "E70.2.4.2", {"start": v(25.4, -12.7) * mm, "end": v(25.4, 12.7) * mm});
            skLineSegment(sketch, "E70.2.4.3", {"start": v(25.4, 12.7) * mm, "end": v(31.75, 12.7) * mm});
            skLineSegment(sketch, "E70.2.4.4", {"start": v(25.4, -12.7) * mm, "end": v(31.75, -12.7) * mm});
            skPoint(sketch, "E70.2.5.0", {"position": v(28.57, 38.1) * mm});
            skLineSegment(sketch, "E70.2.5.1", {"start": v(31.75, 38.1) * mm, "end": v(31.75, 63.5) * mm});
            skLineSegment(sketch, "E70.2.5.2", {"start": v(25.4, 38.1) * mm, "end": v(25.4, 63.5) * mm});
            skLineSegment(sketch, "E70.2.5.3", {"start": v(25.4, 63.5) * mm, "end": v(31.75, 63.5) * mm});
            skLineSegment(sketch, "E70.2.5.4", {"start": v(25.4, 38.1) * mm, "end": v(31.75, 38.1) * mm});
            skPoint(sketch, "E70.2.6.0", {"position": v(28.57, 88.9) * mm});
            skLineSegment(sketch, "E70.2.6.1", {"start": v(31.75, 88.9) * mm, "end": v(31.75, 114.3) * mm});
            skLineSegment(sketch, "E70.2.6.2", {"start": v(25.4, 88.9) * mm, "end": v(25.4, 114.3) * mm});
            skLineSegment(sketch, "E70.2.6.3", {"start": v(25.4, 114.3) * mm, "end": v(31.75, 114.3) * mm});
            skLineSegment(sketch, "E70.2.6.4", {"start": v(25.4, 88.9) * mm, "end": v(31.75, 88.9) * mm});
            skPoint(sketch, "E70.2.7.0", {"position": v(28.57, 139.7) * mm});
            skLineSegment(sketch, "E70.2.7.1", {"start": v(31.75, 139.7) * mm, "end": v(31.75, 165.1) * mm});
            skLineSegment(sketch, "E70.2.7.2", {"start": v(25.4, 139.7) * mm, "end": v(25.4, 165.1) * mm});
            skLineSegment(sketch, "E70.2.7.3", {"start": v(25.4, 165.1) * mm, "end": v(31.75, 165.1) * mm});
            skLineSegment(sketch, "E70.2.7.4", {"start": v(25.4, 139.7) * mm, "end": v(31.75, 139.7) * mm});
            skPoint(sketch, "E70.2.8.0", {"position": v(28.57, 190.5) * mm});
            skLineSegment(sketch, "E70.2.8.1", {"start": v(31.75, 190.5) * mm, "end": v(31.75, 215.9) * mm});
            skLineSegment(sketch, "E70.2.8.2", {"start": v(25.4, 190.5) * mm, "end": v(25.4, 215.9) * mm});
            skLineSegment(sketch, "E70.2.8.3", {"start": v(25.4, 215.9) * mm, "end": v(31.75, 215.9) * mm});
            skLineSegment(sketch, "E70.2.8.4", {"start": v(25.4, 190.5) * mm, "end": v(31.75, 190.5) * mm});
            skPoint(sketch, "E70.3.0.0", {"position": v(92.07, -215.9) * mm});
            skLineSegment(sketch, "E70.3.0.1", {"start": v(95.25, -215.9) * mm, "end": v(95.25, -190.5) * mm});
            skLineSegment(sketch, "E70.3.0.2", {"start": v(88.9, -215.9) * mm, "end": v(88.9, -190.5) * mm});
            skLineSegment(sketch, "E70.3.0.3", {"start": v(88.9, -190.5) * mm, "end": v(95.25, -190.5) * mm});
            skLineSegment(sketch, "E70.3.0.4", {"start": v(88.9, -215.9) * mm, "end": v(95.25, -215.9) * mm});
            skPoint(sketch, "E70.3.1.0", {"position": v(92.07, -165.1) * mm});
            skLineSegment(sketch, "E70.3.1.1", {"start": v(95.25, -165.1) * mm, "end": v(95.25, -139.7) * mm});
            skLineSegment(sketch, "E70.3.1.2", {"start": v(88.9, -165.1) * mm, "end": v(88.9, -139.7) * mm});
            skLineSegment(sketch, "E70.3.1.3", {"start": v(88.9, -139.7) * mm, "end": v(95.25, -139.7) * mm});
            skLineSegment(sketch, "E70.3.1.4", {"start": v(88.9, -165.1) * mm, "end": v(95.25, -165.1) * mm});
            skPoint(sketch, "E70.3.2.0", {"position": v(92.07, -114.3) * mm});
            skLineSegment(sketch, "E70.3.2.1", {"start": v(95.25, -114.3) * mm, "end": v(95.25, -88.9) * mm});
            skLineSegment(sketch, "E70.3.2.2", {"start": v(88.9, -114.3) * mm, "end": v(88.9, -88.9) * mm});
            skLineSegment(sketch, "E70.3.2.3", {"start": v(88.9, -88.9) * mm, "end": v(95.25, -88.9) * mm});
            skLineSegment(sketch, "E70.3.2.4", {"start": v(88.9, -114.3) * mm, "end": v(95.25, -114.3) * mm});
            skPoint(sketch, "E70.3.3.0", {"position": v(92.07, -63.5) * mm});
            skLineSegment(sketch, "E70.3.3.1", {"start": v(95.25, -63.5) * mm, "end": v(95.25, -38.1) * mm});
            skLineSegment(sketch, "E70.3.3.2", {"start": v(88.9, -63.5) * mm, "end": v(88.9, -38.1) * mm});
            skLineSegment(sketch, "E70.3.3.3", {"start": v(88.9, -38.1) * mm, "end": v(95.25, -38.1) * mm});
            skLineSegment(sketch, "E70.3.3.4", {"start": v(88.9, -63.5) * mm, "end": v(95.25, -63.5) * mm});
            skPoint(sketch, "E70.3.4.0", {"position": v(92.07, -12.7) * mm});
            skLineSegment(sketch, "E70.3.4.1", {"start": v(95.25, -12.7) * mm, "end": v(95.25, 12.7) * mm});
            skLineSegment(sketch, "E70.3.4.2", {"start": v(88.9, -12.7) * mm, "end": v(88.9, 12.7) * mm});
            skLineSegment(sketch, "E70.3.4.3", {"start": v(88.9, 12.7) * mm, "end": v(95.25, 12.7) * mm});
            skLineSegment(sketch, "E70.3.4.4", {"start": v(88.9, -12.7) * mm, "end": v(95.25, -12.7) * mm});
            skPoint(sketch, "E70.3.5.0", {"position": v(92.07, 38.1) * mm});
            skLineSegment(sketch, "E70.3.5.1", {"start": v(95.25, 38.1) * mm, "end": v(95.25, 63.5) * mm});
            skLineSegment(sketch, "E70.3.5.2", {"start": v(88.9, 38.1) * mm, "end": v(88.9, 63.5) * mm});
            skLineSegment(sketch, "E70.3.5.3", {"start": v(88.9, 63.5) * mm, "end": v(95.25, 63.5) * mm});
            skLineSegment(sketch, "E70.3.5.4", {"start": v(88.9, 38.1) * mm, "end": v(95.25, 38.1) * mm});
            skPoint(sketch, "E70.3.6.0", {"position": v(92.07, 88.9) * mm});
            skLineSegment(sketch, "E70.3.6.1", {"start": v(95.25, 88.9) * mm, "end": v(95.25, 114.3) * mm});
            skLineSegment(sketch, "E70.3.6.2", {"start": v(88.9, 88.9) * mm, "end": v(88.9, 114.3) * mm});
            skLineSegment(sketch, "E70.3.6.3", {"start": v(88.9, 114.3) * mm, "end": v(95.25, 114.3) * mm});
            skLineSegment(sketch, "E70.3.6.4", {"start": v(88.9, 88.9) * mm, "end": v(95.25, 88.9) * mm});
            skPoint(sketch, "E70.3.7.0", {"position": v(92.07, 139.7) * mm});
            skLineSegment(sketch, "E70.3.7.1", {"start": v(95.25, 139.7) * mm, "end": v(95.25, 165.1) * mm});
            skLineSegment(sketch, "E70.3.7.2", {"start": v(88.9, 139.7) * mm, "end": v(88.9, 165.1) * mm});
            skLineSegment(sketch, "E70.3.7.3", {"start": v(88.9, 165.1) * mm, "end": v(95.25, 165.1) * mm});
            skLineSegment(sketch, "E70.3.7.4", {"start": v(88.9, 139.7) * mm, "end": v(95.25, 139.7) * mm});
            skPoint(sketch, "E70.3.8.0", {"position": v(92.07, 190.5) * mm});
            skLineSegment(sketch, "E70.3.8.1", {"start": v(95.25, 190.5) * mm, "end": v(95.25, 215.9) * mm});
            skLineSegment(sketch, "E70.3.8.2", {"start": v(88.9, 190.5) * mm, "end": v(88.9, 215.9) * mm});
            skLineSegment(sketch, "E70.3.8.3", {"start": v(88.9, 215.9) * mm, "end": v(95.25, 215.9) * mm});
            skLineSegment(sketch, "E70.3.8.4", {"start": v(88.9, 190.5) * mm, "end": v(95.25, 190.5) * mm});
            skLineSegment(sketch, "E70.direction1", {"start": v(-98.43, -215.9) * mm, "end": v(-34.93, -215.9) * mm, "construction": true});
            skLineSegment(sketch, "E70.direction2", {"start": v(-98.43, -215.9) * mm, "end": v(-98.43, -165.1) * mm, "construction": true});
            skPoint(sketch, "E71", {"position": v(-161.93, -215.9) * mm});
            skSolve(sketch);
        }
        {
            var Q0;
            Q0 = qSketchRegion(id + "F4", true);
            extrude(context, id + "F5", {"entities" : qUnion([Q0]), "operationType" : NewBodyOperationType.REMOVE, "endBound" : BoundingType.UP_TO_NEXT, "oppositeDirection" : true, "depth" : 25.4 * mm});
        }
    });
